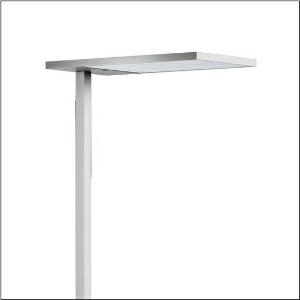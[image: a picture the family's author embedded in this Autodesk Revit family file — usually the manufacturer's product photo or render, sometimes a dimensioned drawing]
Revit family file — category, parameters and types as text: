
# Revit family: silica_21_floor_r_51mx53sg4es
name_source: partatom
category: Lighting Fixtures
units: mm (PartAtom-declared; Revit-internal decimal feet)

## family parameters
Cut with Voids When Loaded = No
Host = Face
Light Source = No
Part Type = Normal
Room Calculation Point = No
Round Connector Dimension = Use Diameter
Shared = No

## types (1)
- Silica 21 Floor R (1 x LED, 15000 lm, 106.4 W, 4000K)
    Apparent Load = 106 VA
    CIE Flux Codes = 54 86 97 13 100
    Color Rendering = 80
    Color Temperature = 4000K
    Default Elevation = 1800 mm
    Description = Silica® 21 Floor R, floorstanding luminaire, of PMMA, primary optical cover: prismatic diffuser, of PMMA, CAT 2 (L<= 3000cd/m²), light emission: indirect/direct distribution, primary light characteristic: symmetric, primary optical cover: cover panel, of PMMA, installation type: not mounted, LED, rated luminous flux: 15.000lm, luminous efficacy: 141lm/W, light colour: 840, colour temperature: 4000K, control gear: DALI 2, daylight-dependent control, mains connection: 230V, AC, 50/60Hz, connection cable included, cable length: 2,5m, rated input power: 106.4W, luminaire head, of aluminium, powder-coated, metallic grey (RAL 9006), length: 671mm, width: 371mm, height: 2010mm, supporting column, angular, of aluminium, powder-coated, metallic grey (RAL 9006), baseplate, of steel, powder-coated, metallic grey (RAL 9006), sensor module PR3-S, local control - self-sufficient standalone sensors, equipment: master, direct and indirect component separately switchable, protection rating (complete): IP20, insulation class (complete): insulation class I (protective earthing), certification: CE, permissible operating ambient temperature: 0..+35°C, standard: EN 50419, packaging unit: 1 piece
    Height = 18 mm
    Lamp = 1 x LED
    Lamp Light Flux = 15000 lm
    Lamp Power = 106.4 W
    Lamp count = 1
    Length = 650 mm
    Luminous efficacy = 141 lm/W
    Manufacturer = Siteco
    ModVariant = No
    Model = 51MX53SG4ES
    Mounting Place = Floor
    Mounting Type = Freestanding
    Number of Poles = 1
    OnlyDefault = Yes
    Power Factor = 1
    Product Name = Silica 21 Floor R
    Product group = floorstanding luminaire
    ProductGroupID = 1302
    Protection Class = Protection class I
    Protection Degree = IP 20
    RLX_Detail_Level = 1
    RLX_Emergency_Light_Flux = 0 lm
    RLX_Emergency_Type = 0
    RLX_Emergency_Type_DB = No
    RlxData = <blob elided: 20509 chars, md5=e99ef9bb>
    Socket = socket
    Standby Power = 0 W
    System Light Flux = 15000 lm
    System Power = 106 W
    Type Comments = Product without accessories
    Type Image = l_1006716.jpg
    URL = http://relux.com
    VarID = ---
    Voltage = 0 V
    Weight = 0.00 kg
    Width = 350 mm

## geometry (parser evidence)
native form markers: Blend x4, Sweep x13
no freeform markers — native parametric forms only
